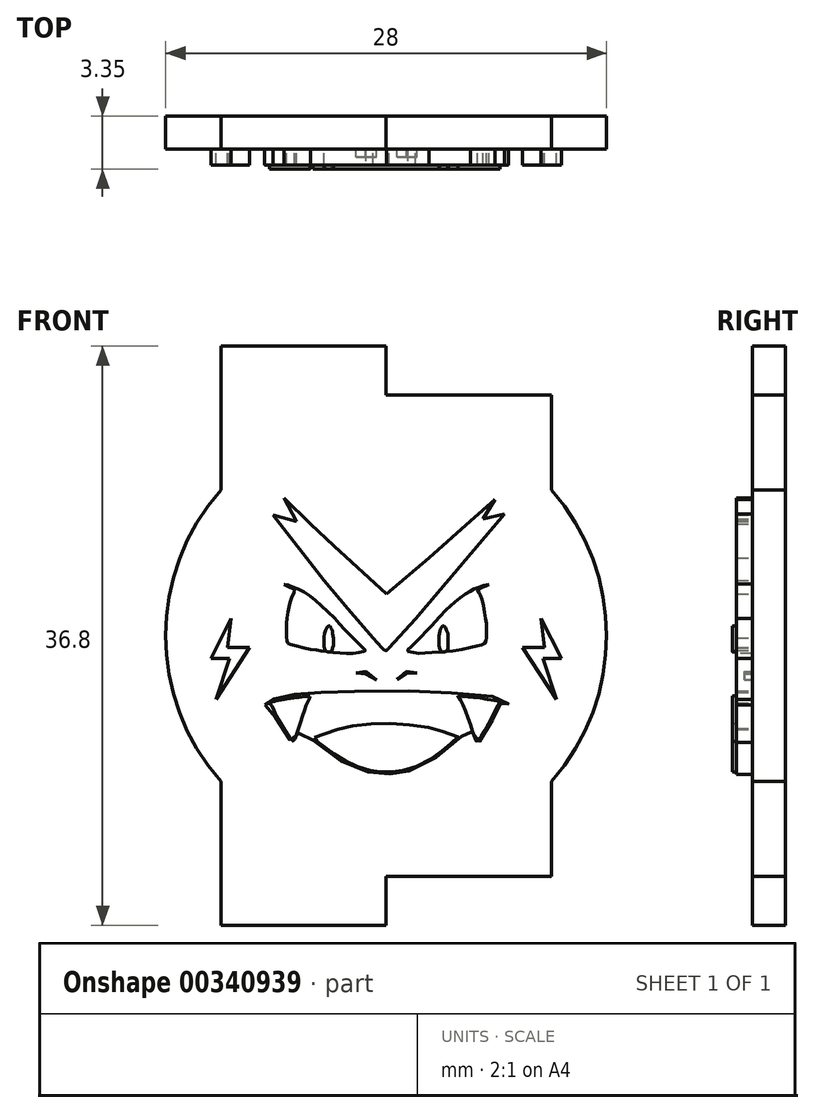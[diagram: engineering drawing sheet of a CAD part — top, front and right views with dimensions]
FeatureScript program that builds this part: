
annotation { "Feature Type Name" : "Feature", "Feature Type Description" : "" }
export const myFeature = defineFeature(function(context is Context, id is Id, definition is map)
    precondition{}
    {
        {
            var Q0;
            Q0=qCreatedBy(makeId("Front.planeOp"),FACE);
            var sketch = newSketch(context, id + "F0", { "sketchPlane" : qUnion([Q0])});
            skArc(sketch, "E0", {"start": v(10.5, -9.26) * mm, "mid": v(14, 0) * mm, "end": v(10.5, 9.26) * mm});
            skLineSegment(sketch, "E1", {"start": v(-10.5, -9.26) * mm, "end": v(-10.5, -18.4) * mm});
            skLineSegment(sketch, "E2", {"start": v(-10.5, -18.4) * mm, "end": v(0, -18.4) * mm});
            skLineSegment(sketch, "E3", {"start": v(0, -18.4) * mm, "end": v(0, -15.3) * mm});
            skLineSegment(sketch, "E4", {"start": v(0, -15.3) * mm, "end": v(10.5, -15.3) * mm});
            skLineSegment(sketch, "E5", {"start": v(10.5, -15.3) * mm, "end": v(10.5, -9.26) * mm});
            skLineSegment(sketch, "E6.MirrorCS", {"start": v(-10.5, 9.26) * mm, "end": v(-10.5, 18.4) * mm});
            skLineSegment(sketch, "E7.MirrorCS", {"start": v(-10.5, 18.4) * mm, "end": v(0, 18.4) * mm});
            skLineSegment(sketch, "E8.MirrorCS", {"start": v(0, 15.3) * mm, "end": v(10.5, 15.3) * mm});
            skLineSegment(sketch, "E9.MirrorCS", {"start": v(0, 18.4) * mm, "end": v(0, 15.3) * mm});
            skLineSegment(sketch, "E10.MirrorCS", {"start": v(10.5, 15.3) * mm, "end": v(10.5, 9.26) * mm});
            skArc(sketch, "E11.trimOffspring", {"start": v(-10.5, 9.26) * mm, "mid": v(-14, 0) * mm, "end": v(-10.5, -9.26) * mm});
            skSolve(sketch);
        }
        {
            var Q0;
            Q0 = qSketchRegion(id + "F0", true);
            extrude(context, id + "F1", {"entities" : qUnion([Q0]), "depth" : 2.1 * mm});
        }
        {
            var Q0;
            Q0=makeQuery(id+"F1.opExtrude","CAP_FACE",FACE,{"disambiguationData":[OSD([sQuery(id+"F0.wireOp",EDGE,"E0"),sQuery(id+"F0.wireOp",EDGE,"E1"),sQuery(id+"F0.wireOp",EDGE,"E2"),sQuery(id+"F0.wireOp",EDGE,"E3"),sQuery(id+"F0.wireOp",EDGE,"E4"),sQuery(id+"F0.wireOp",EDGE,"E5"),sQuery(id+"F0.wireOp",EDGE,"E6.MirrorCS"),sQuery(id+"F0.wireOp",EDGE,"E7.MirrorCS"),sQuery(id+"F0.wireOp",EDGE,"E8.MirrorCS"),sQuery(id+"F0.wireOp",EDGE,"E9.MirrorCS"),sQuery(id+"F0.wireOp",EDGE,"E10.MirrorCS"),sQuery(id+"F0.wireOp",EDGE,"E11.trimOffspring")])],"isStart":false});
            var sketch = newSketch(context, id + "F2", { "sketchPlane" : qUnion([Q0])});
            skPoint(sketch, "E12", {"position": v(10.5, -12.28) * mm});
            skLineSegment(sketch, "E13", {"start": v(-7.17, 7.67) * mm, "end": v(-5.12, 5.04) * mm});
            skLineSegment(sketch, "E14", {"start": v(-5.12, 5.04) * mm, "end": v(-3.93, 3.51) * mm});
            skLineSegment(sketch, "E15", {"start": v(-3.93, 3.51) * mm, "end": v(-2.41, 1.7) * mm});
            skLineSegment(sketch, "E16", {"start": v(-2.41, 1.7) * mm, "end": v(-0.84, -0.15) * mm});
            skLineSegment(sketch, "E17", {"start": v(-0.84, -0.15) * mm, "end": v(-0.26, -0.78) * mm});
            skFitSpline(sketch, "E18", {"points": [v(-0.26, -0.78) * mm, v(-0.14, -0.9) * mm, v(0, -0.94) * mm, v(0.18, -0.78) * mm], "startDerivative": vector(0.35, -0.37) * mm, "endDerivative": vector(0.46, 0.56) * mm});
            skLineSegment(sketch, "E19", {"start": v(0.18, -0.78) * mm, "end": v(1.86, 1.06) * mm});
            skLineSegment(sketch, "E20", {"start": v(1.86, 1.06) * mm, "end": v(4.38, 4.04) * mm});
            skLineSegment(sketch, "E21", {"start": v(4.38, 4.04) * mm, "end": v(7.52, 7.74) * mm});
            skLineSegment(sketch, "E22", {"start": v(7.52, 7.74) * mm, "end": v(6.14, 7.41) * mm});
            skLineSegment(sketch, "E23", {"start": v(6.14, 7.41) * mm, "end": v(6.92, 8.65) * mm});
            skLineSegment(sketch, "E24", {"start": v(6.92, 8.65) * mm, "end": v(5.36, 7.29) * mm});
            skLineSegment(sketch, "E25", {"start": v(5.36, 7.29) * mm, "end": v(2.72, 4.94) * mm});
            skLineSegment(sketch, "E26", {"start": v(2.72, 4.94) * mm, "end": v(0.03, 2.65) * mm});
            skLineSegment(sketch, "E27", {"start": v(0.03, 2.65) * mm, "end": v(-3.3, 5.7) * mm});
            skLineSegment(sketch, "E28", {"start": v(-3.3, 5.7) * mm, "end": v(-4.82, 7.09) * mm});
            skLineSegment(sketch, "E29", {"start": v(-4.82, 7.09) * mm, "end": v(-6.5, 8.74) * mm});
            skLineSegment(sketch, "E30", {"start": v(-6.5, 8.74) * mm, "end": v(-5.7, 7.26) * mm});
            skLineSegment(sketch, "E31", {"start": v(-5.7, 7.26) * mm, "end": v(-7.17, 7.67) * mm});
            skFitSpline(sketch, "E32", {"points": [v(-7.7, -4.4) * mm, v(-7.67, -4.26) * mm, v(-7.54, -4.18) * mm, v(-7.14, -4.03) * mm, v(-6.43, -3.85) * mm, v(-5.6, -3.7) * mm, v(-4.18, -3.6) * mm, v(-3.96, -3.6) * mm, v(0.24, -3.5) * mm, v(3.75, -3.62) * mm, v(6.81, -3.87) * mm, v(7.68, -4.14) * mm, v(7.76, -4.3) * mm, v(7.7, -4.38) * mm, v(7.55, -4.33) * mm, v(7.42, -4.28) * mm, v(7.3, -4.28) * mm, v(7.27, -4.41) * mm, v(7.02, -4.84) * mm, v(6.48, -5.92) * mm, v(5.93, -6.72) * mm, v(5.68, -6.76) * mm, v(5.51, -6.43) * mm, v(5.36, -5.93) * mm, v(5.3, -5.9) * mm, v(4.94, -6.25) * mm, v(3.56, -7.46) * mm, v(1.98, -8.39) * mm, v(0.9, -8.72) * mm, v(0.35, -8.77) * mm, v(-0.12, -8.8) * mm, v(-1.24, -8.62) * mm, v(-2.66, -8.06) * mm, v(-4.2, -7.02) * mm, v(-5.42, -5.96) * mm, v(-5.49, -6.08) * mm, v(-5.67, -6.58) * mm, v(-5.86, -6.78) * mm, v(-6.42, -6.24) * mm, v(-7.07, -5.1) * mm, v(-7.42, -4.42) * mm, v(-7.7, -4.4) * mm]});
            skLineSegment(sketch, "E33", {"start": v(-1.92, -2.37) * mm, "end": v(-1.28, -2.29) * mm});
            skLineSegment(sketch, "E34", {"start": v(-1.28, -2.29) * mm, "end": v(-0.62, -2.81) * mm});
            skLineSegment(sketch, "E35", {"start": v(-0.62, -2.81) * mm, "end": v(-1.3, -2.42) * mm});
            skLineSegment(sketch, "E36", {"start": v(-1.3, -2.42) * mm, "end": v(-1.92, -2.37) * mm});
            skLineSegment(sketch, "E37", {"start": v(0.7, -2.77) * mm, "end": v(1.3, -2.26) * mm});
            skLineSegment(sketch, "E38", {"start": v(1.3, -2.26) * mm, "end": v(1.96, -2.37) * mm});
            skLineSegment(sketch, "E39", {"start": v(1.96, -2.37) * mm, "end": v(1.32, -2.37) * mm});
            skLineSegment(sketch, "E40", {"start": v(1.32, -2.37) * mm, "end": v(0.7, -2.77) * mm});
            skFitSpline(sketch, "E41", {"points": [v(-6.5, 3.26) * mm, v(-6.3, 3.24) * mm, v(-6.03, 3.14) * mm, v(-5.64, 2.98) * mm, v(-5.16, 2.73) * mm, v(-4.66, 2.39) * mm, v(-4.15, 1.95) * mm, v(-3.37, 1.2) * mm, v(-2.89, 0.67) * mm, v(-2.41, 0.16) * mm, v(-1.99, -0.27) * mm, v(-1.6, -0.65) * mm, v(-1.39, -0.87) * mm, v(-1.33, -0.92) * mm, v(-1.32, -0.97) * mm, v(-1.38, -1) * mm, v(-1.46, -1.02) * mm, v(-1.8, -1.08) * mm, v(-2.25, -1.12) * mm, v(-2.77, -1.1) * mm, v(-3.32, -1.08) * mm, v(-3.95, -1) * mm, v(-4.41, -0.92) * mm, v(-5.2, -0.78) * mm, v(-6.12, -0.53) * mm, v(-6.22, -0.5) * mm, v(-6.3, -0.37) * mm, v(-6.33, -0.1) * mm, v(-6.34, 0.45) * mm, v(-6.33, 0.78) * mm, v(-6.25, 1.42) * mm, v(-6.14, 1.97) * mm, v(-5.99, 2.43) * mm, v(-5.8, 2.9) * mm, v(-5.84, 2.95) * mm, v(-5.98, 3.02) * mm, v(-6.2, 3.12) * mm, v(-6.41, 3.22) * mm, v(-6.5, 3.26) * mm]});
            skFitSpline(sketch, "E42", {"points": [v(6.52, 3.27) * mm, v(6.07, 3.16) * mm, v(5.77, 3.04) * mm, v(5.47, 2.9) * mm, v(5.12, 2.7) * mm, v(4.72, 2.42) * mm, v(4.24, 2.04) * mm, v(3.7, 1.5) * mm, v(2.75, 0.5) * mm, v(2.4, 0.12) * mm, v(1.98, -0.32) * mm, v(1.68, -0.6) * mm, v(1.48, -0.8) * mm, v(1.36, -0.9) * mm, v(1.36, -0.97) * mm, v(1.52, -1.03) * mm, v(2.05, -1.11) * mm, v(2.65, -1.1) * mm, v(3.49, -1.04) * mm, v(3.96, -1) * mm, v(5.56, -0.72) * mm, v(6.11, -0.56) * mm, v(6.27, -0.49) * mm, v(6.36, -0.22) * mm, v(6.37, 0) * mm, v(6.37, 0.67) * mm, v(6.29, 1.33) * mm, v(6.2, 1.78) * mm, v(5.99, 2.56) * mm, v(5.83, 2.86) * mm, v(5.8, 2.9) * mm, v(5.8, 2.95) * mm, v(5.9, 2.97) * mm, v(5.94, 3) * mm, v(6.09, 3.06) * mm, v(6.3, 3.15) * mm, v(6.52, 3.27) * mm]});
            skPoint(sketch, "E43.26.internal.orphan", {"position": v(-3.47, -7.46) * mm});
            skPoint(sketch, "E43.28.internal.orphan", {"position": v(-4.2, -6.9) * mm});
            skSolve(sketch);
        }
        {
            var Q0;
            Q0=makeQuery(id+"F2.imprint","IMPRINT",FACE,{"disambiguationData":[TD([[makeQuery(id+"F2.imprint","IMPRINT",EDGE,{"derivedFrom":sQuery(id+"F2.wireOp",EDGE,"E41")}),-1.0]])]});
            var Q1;
            Q1=makeQuery(id+"F2.imprint","IMPRINT",FACE,{"disambiguationData":[TD([[makeQuery(id+"F2.imprint","IMPRINT",EDGE,{"derivedFrom":sQuery(id+"F2.wireOp",EDGE,"E13")}),1.0]])]});
            var Q2;
            Q2=makeQuery(id+"F2.imprint","IMPRINT",FACE,{"disambiguationData":[TD([[makeQuery(id+"F2.imprint","IMPRINT",EDGE,{"derivedFrom":sQuery(id+"F2.wireOp",EDGE,"E42")}),1.0]])]});
            var Q3;
            Q3=makeQuery(id+"F2.imprint","IMPRINT",FACE,{"disambiguationData":[TD([[makeQuery(id+"F2.imprint","IMPRINT",EDGE,{"derivedFrom":sQuery(id+"F2.wireOp",EDGE,"E32")}),-1.0]])]});
            extrude(context, id + "F3", {"entities" : qUnion([Q0, Q1, Q2, Q3]), "operationType" : NewBodyOperationType.ADD, "depth" : 1 * mm});
        }
        {
            var Q0;
            Q0=makeQuery(id+"F3.opExtrude","CAP_FACE",FACE,{"disambiguationData":[OSD([sQuery(id+"F2.wireOp",EDGE,"E32")])],"isStart":false});
            var sketch = newSketch(context, id + "F4", { "sketchPlane" : qUnion([Q0])});
            skFitSpline(sketch, "E44", {"points": [v(-4.56, -6.47) * mm, v(-4.2, -6.34) * mm, v(-3.67, -6.15) * mm, v(-3, -5.92) * mm, v(-2.19, -5.75) * mm, v(-0.93, -5.62) * mm, v(0.38, -5.58) * mm, v(1.74, -5.69) * mm, v(2.94, -5.9) * mm, v(3.66, -6.1) * mm, v(4.57, -6.43) * mm, v(4.47, -6.54) * mm, v(4.09, -6.89) * mm, v(3.74, -7.17) * mm, v(3.26, -7.52) * mm, v(2.65, -7.94) * mm, v(1.72, -8.38) * mm, v(1.11, -8.56) * mm, v(0.67, -8.65) * mm, v(0.14, -8.66) * mm, v(-0.29, -8.66) * mm, v(-0.7, -8.62) * mm, v(-1.12, -8.53) * mm, v(-1.79, -8.33) * mm, v(-2.29, -8.1) * mm, v(-2.88, -7.8) * mm, v(-3.43, -7.45) * mm, v(-3.8, -7.16) * mm, v(-4.17, -6.88) * mm, v(-4.36, -6.74) * mm, v(-4.5, -6.62) * mm, v(-4.64, -6.5) * mm, v(-4.56, -6.47) * mm]});
            skFitSpline(sketch, "E45", {"points": [v(-3.83, -1) * mm, v(-3.87, -0.94) * mm, v(-3.9, -0.87) * mm, v(-3.93, -0.8) * mm, v(-3.94, -0.7) * mm, v(-3.94, -0.57) * mm, v(-3.94, -0.45) * mm, v(-3.94, -0.32) * mm, v(-3.94, -0.2) * mm, v(-3.93, 0.04) * mm, v(-3.84, 0.35) * mm, v(-3.75, 0.53) * mm, v(-3.68, 0.6) * mm, v(-3.63, 0.61) * mm, v(-3.57, 0.6) * mm, v(-3.54, 0.54) * mm, v(-3.5, 0.48) * mm, v(-3.45, 0.39) * mm, v(-3.42, 0.29) * mm, v(-3.4, 0.16) * mm, v(-3.37, 0) * mm, v(-3.36, -0.13) * mm, v(-3.35, -0.51) * mm, v(-3.37, -0.7) * mm, v(-3.43, -0.87) * mm, v(-3.47, -1) * mm, v(-3.5, -1.04) * mm], "startDerivative": vector(-1.67, 1.95) * mm, "endDerivative": vector(-1.05, -1.6) * mm});
            skFitSpline(sketch, "E46", {"points": [v(-3.83, -1) * mm, v(-3.74, -1.02) * mm, v(-3.59, -1.04) * mm, v(-3.5, -1.04) * mm], "startDerivative": vector(0.27, -0.03) * mm, "endDerivative": vector(0.27, -0.02) * mm});
            skPoint(sketch, "E47.MirrorCS.end.orphan", {"position": v(3.5, -1.04) * mm});
            skPoint(sketch, "E47.MirrorCS.start.orphan", {"position": v(3.83, -1) * mm});
            skFitSpline(sketch, "E48.MirrorCS", {"points": [v(3.83, -1) * mm, v(3.74, -1.02) * mm, v(3.59, -1.04) * mm, v(3.5, -1.04) * mm], "startDerivative": vector(-0.27, -0.03) * mm, "endDerivative": vector(-0.27, -0.02) * mm});
            skFitSpline(sketch, "E49.MirrorCS", {"points": [v(3.83, -1) * mm, v(3.87, -0.94) * mm, v(3.9, -0.87) * mm, v(3.93, -0.8) * mm, v(3.94, -0.7) * mm, v(3.94, -0.57) * mm, v(3.94, -0.45) * mm, v(3.94, -0.32) * mm, v(3.94, -0.2) * mm, v(3.93, 0.04) * mm, v(3.84, 0.35) * mm, v(3.75, 0.53) * mm, v(3.68, 0.6) * mm, v(3.63, 0.61) * mm, v(3.57, 0.6) * mm, v(3.54, 0.54) * mm, v(3.5, 0.48) * mm, v(3.45, 0.39) * mm, v(3.42, 0.29) * mm, v(3.4, 0.16) * mm, v(3.37, 0) * mm, v(3.36, -0.13) * mm, v(3.35, -0.51) * mm, v(3.37, -0.7) * mm, v(3.43, -0.87) * mm, v(3.47, -1) * mm, v(3.5, -1.04) * mm], "startDerivative": vector(1.67, 1.95) * mm, "endDerivative": vector(1.05, -1.6) * mm});
            skFitSpline(sketch, "E50", {"points": [v(-4.83, -3.86) * mm, v(-4.84, -3.92) * mm, v(-4.9, -4.02) * mm, v(-5.03, -4.3) * mm, v(-5.2, -4.77) * mm, v(-5.47, -5.61) * mm, v(-5.87, -6.69) * mm, v(-5.95, -6.66) * mm, v(-6.55, -5.82) * mm, v(-7.1, -4.82) * mm, v(-7.3, -4.4) * mm, v(-7.4, -4.3) * mm, v(-6.4, -4.02) * mm, v(-5.53, -3.9) * mm, v(-4.98, -3.86) * mm, v(-4.83, -3.86) * mm]});
            skFitSpline(sketch, "E51", {"points": [v(4.55, -3.84) * mm, v(4.69, -3.84) * mm, v(5, -3.86) * mm, v(5.32, -3.9) * mm, v(5.65, -3.93) * mm, v(6.06, -3.98) * mm, v(6.57, -4.06) * mm, v(7.03, -4.14) * mm, v(7.22, -4.2) * mm, v(7.2, -4.25) * mm, v(7.08, -4.47) * mm, v(6.93, -4.74) * mm, v(6.69, -5.25) * mm, v(6.47, -5.67) * mm, v(6.17, -6.2) * mm, v(6, -6.47) * mm, v(5.85, -6.65) * mm, v(5.8, -6.7) * mm, v(5.74, -6.71) * mm, v(5.71, -6.7) * mm, v(5.68, -6.64) * mm, v(5.58, -6.34) * mm, v(5.42, -5.89) * mm, v(5.26, -5.4) * mm, v(5.09, -4.94) * mm, v(4.9, -4.48) * mm, v(4.8, -4.23) * mm, v(4.65, -3.97) * mm, v(4.55, -3.84) * mm]});
            skSolve(sketch);
        }
        {
            var Q0;
            Q0=makeQuery(id+"F4.imprint","IMPRINT",FACE,{"disambiguationData":[TD([[makeQuery(id+"F4.imprint","IMPRINT",EDGE,{"derivedFrom":sQuery(id+"F4.wireOp",EDGE,"E45")}),-1.0]])]});
            var Q1;
            Q1=makeQuery(id+"F4.imprint","IMPRINT",FACE,{"disambiguationData":[TD([[makeQuery(id+"F4.imprint","IMPRINT",EDGE,{"derivedFrom":sQuery(id+"F4.wireOp",EDGE,"E48.MirrorCS")}),-1.0]])]});
            var Q2;
            Q2=makeQuery(id+"F4.imprint","IMPRINT",FACE,{"disambiguationData":[TD([[makeQuery(id+"F4.imprint","IMPRINT",EDGE,{"derivedFrom":sQuery(id+"F4.wireOp",EDGE,"E44")}),-1.0]])]});
            var Q3;
            Q3=makeQuery(id+"F4.imprint","IMPRINT",FACE,{"disambiguationData":[TD([[makeQuery(id+"F4.imprint","IMPRINT",EDGE,{"derivedFrom":sQuery(id+"F4.wireOp",EDGE,"E50")}),-1.0]])]});
            var Q4;
            Q4=makeQuery(id+"F4.imprint","IMPRINT",FACE,{"disambiguationData":[TD([[makeQuery(id+"F4.imprint","IMPRINT",EDGE,{"derivedFrom":sQuery(id+"F4.wireOp",EDGE,"E51")}),-1.0]])]});
            extrude(context, id + "F5", {"entities" : qUnion([Q0, Q1, Q2, Q3, Q4]), "operationType" : NewBodyOperationType.ADD, "depth" : 0.25 * mm});
        }
        {
            var Q0;
            Q0=makeQuery(id+"F1.opExtrude","CAP_FACE",FACE,{"disambiguationData":[OSD([sQuery(id+"F0.wireOp",EDGE,"E0"),sQuery(id+"F0.wireOp",EDGE,"E1"),sQuery(id+"F0.wireOp",EDGE,"E2"),sQuery(id+"F0.wireOp",EDGE,"E3"),sQuery(id+"F0.wireOp",EDGE,"E4"),sQuery(id+"F0.wireOp",EDGE,"E5"),sQuery(id+"F0.wireOp",EDGE,"E6.MirrorCS"),sQuery(id+"F0.wireOp",EDGE,"E7.MirrorCS"),sQuery(id+"F0.wireOp",EDGE,"E8.MirrorCS"),sQuery(id+"F0.wireOp",EDGE,"E9.MirrorCS"),sQuery(id+"F0.wireOp",EDGE,"E10.MirrorCS"),sQuery(id+"F0.wireOp",EDGE,"E11.trimOffspring")])],"isStart":false});
            var sketch = newSketch(context, id + "F6", { "sketchPlane" : qUnion([Q0])});
            skLineSegment(sketch, "E52", {"start": v(-9.84, 1.09) * mm, "end": v(-11.13, -1.45) * mm});
            skLineSegment(sketch, "E53", {"start": v(-11.13, -1.45) * mm, "end": v(-9.96, -1.45) * mm});
            skLineSegment(sketch, "E54", {"start": v(-9.96, -1.45) * mm, "end": v(-10.82, -4.04) * mm});
            skLineSegment(sketch, "E55", {"start": v(-10.82, -4.04) * mm, "end": v(-8.67, -0.75) * mm});
            skLineSegment(sketch, "E56", {"start": v(-8.67, -0.75) * mm, "end": v(-10.07, -0.75) * mm});
            skLineSegment(sketch, "E57", {"start": v(-10.07, -0.75) * mm, "end": v(-9.84, 1.09) * mm});
            skLineSegment(sketch, "E58.MirrorCS", {"start": v(8.67, -0.75) * mm, "end": v(10.07, -0.75) * mm});
            skLineSegment(sketch, "E59.MirrorCS", {"start": v(10.07, -0.75) * mm, "end": v(9.84, 1.09) * mm});
            skLineSegment(sketch, "E60.MirrorCS", {"start": v(9.84, 1.09) * mm, "end": v(11.13, -1.45) * mm});
            skLineSegment(sketch, "E61.MirrorCS", {"start": v(11.13, -1.45) * mm, "end": v(9.96, -1.45) * mm});
            skLineSegment(sketch, "E62.MirrorCS", {"start": v(9.96, -1.45) * mm, "end": v(10.82, -4.04) * mm});
            skLineSegment(sketch, "E63.MirrorCS", {"start": v(10.82, -4.04) * mm, "end": v(8.67, -0.75) * mm});
            skSolve(sketch);
        }
        {
            var Q0;
            Q0=makeQuery(id+"F6.imprint","IMPRINT",FACE,{"disambiguationData":[TD([[makeQuery(id+"F6.imprint","IMPRINT",EDGE,{"derivedFrom":sQuery(id+"F6.wireOp",EDGE,"E52")}),1.0]])]});
            var Q1;
            Q1=makeQuery(id+"F6.imprint","IMPRINT",FACE,{"disambiguationData":[TD([[makeQuery(id+"F6.imprint","IMPRINT",EDGE,{"derivedFrom":sQuery(id+"F6.wireOp",EDGE,"E58.MirrorCS")}),-1.0]])]});
            extrude(context, id + "F7", {"entities" : qUnion([Q0, Q1]), "operationType" : NewBodyOperationType.ADD, "depth" : 1 * mm});
        }
        {
            var Q0;
            Q0=makeQuery(id+"F2.imprint","IMPRINT",FACE,{"disambiguationData":[TD([[makeQuery(id+"F2.imprint","IMPRINT",EDGE,{"derivedFrom":sQuery(id+"F2.wireOp",EDGE,"E33")}),-1.0]])]});
            var Q1;
            Q1=makeQuery(id+"F2.imprint","IMPRINT",FACE,{"disambiguationData":[TD([[makeQuery(id+"F2.imprint","IMPRINT",EDGE,{"derivedFrom":sQuery(id+"F2.wireOp",EDGE,"E37")}),-1.0]])]});
            extrude(context, id + "F8", {"entities" : qUnion([Q0, Q1]), "operationType" : NewBodyOperationType.ADD, "depth" : 0.5 * mm});
        }
    });
